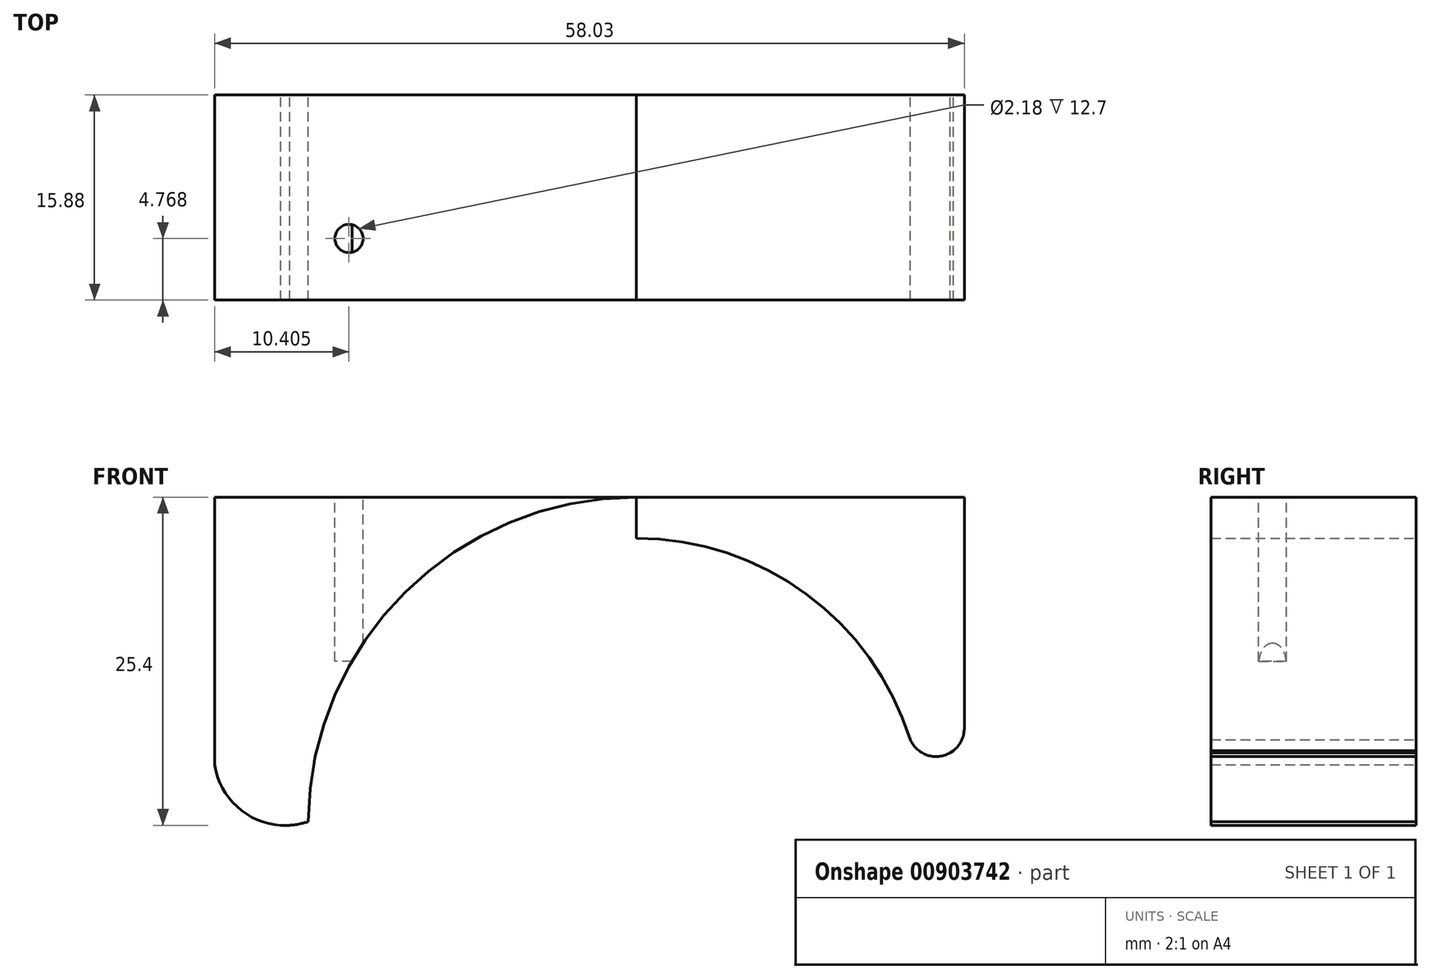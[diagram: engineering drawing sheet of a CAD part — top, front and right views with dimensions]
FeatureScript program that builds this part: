
annotation { "Feature Type Name" : "Feature", "Feature Type Description" : "" }
export const myFeature = defineFeature(function(context is Context, id is Id, definition is map)
    precondition{}
    {
        {
            var Q0;
            Q0=qCreatedBy(makeId("Front.planeOp"),FACE);
            var sketch = newSketch(context, id + "F0", { "sketchPlane" : qUnion([Q0])});
            skCircle(sketch, "E0", {"center": v(0, 0) * mm, "radius": 22.23 * mm});
            skCircle(sketch, "E1", {"center": v(0, 0) * mm, "radius": 25.4 * mm});
            skLineSegment(sketch, "E2.bottom", {"start": v(-25.4, 0) * mm, "end": v(0, 0) * mm});
            skLineSegment(sketch, "E2.top", {"start": v(-25.4, 25.4) * mm, "end": v(0, 25.4) * mm});
            skLineSegment(sketch, "E2.right", {"start": v(0, 0) * mm, "end": v(0, 25.4) * mm});
            skLineSegment(sketch, "E3.bottom", {"start": v(25.4, 0) * mm, "end": v(0, 0) * mm});
            skLineSegment(sketch, "E3.top", {"start": v(25.4, 25.4) * mm, "end": v(0, 25.4) * mm});
            skLineSegment(sketch, "E3.left", {"start": v(25.4, 0) * mm, "end": v(25.4, 25.4) * mm});
            skLineSegment(sketch, "E4", {"start": v(-25.4, 0) * mm, "end": v(-32.63, 0) * mm});
            skLineSegment(sketch, "E5", {"start": v(-32.63, 0) * mm, "end": v(-32.63, 25.4) * mm});
            skLineSegment(sketch, "E6", {"start": v(-32.63, 25.4) * mm, "end": v(-25.4, 25.4) * mm});
            skCircle(sketch, "E7", {"center": v(-27.16, 5.52) * mm, "radius": 5.53 * mm});
            skPoint(sketch, "E7.first.point", {"position": v(-32.63, 4.68) * mm});
            skPoint(sketch, "E7.second.point", {"position": v(-27.5, 0) * mm});
            skPoint(sketch, "E7.third.point", {"position": v(-21.88, 3.87) * mm});
            skLineSegment(sketch, "E8", {"start": v(21.87, 3.98) * mm, "end": v(25.4, 6.34) * mm});
            skCircle(sketch, "E9", {"center": v(23.22, 7.5) * mm, "radius": 2.18 * mm});
            skPoint(sketch, "E9.first.point", {"position": v(25.4, 7.5) * mm});
            skPoint(sketch, "E9.second.point", {"position": v(24.3, 5.6) * mm});
            skPoint(sketch, "E9.third.point", {"position": v(21.08, 7.03) * mm});
            skSolve(sketch);
        }
        {
            var Q0;
            {var subQ0=sQuery(id+"F0.wireOp",EDGE,"E7");var subQ6=sQuery(id+"F0.wireOp",EDGE,"E1");var subQ9=makeQuery(id+"F0.imprint","INTERSECT",VERTEX,{"disambiguationData":[OD(0.0)],"derivedFrom":[subQ6,subQ0]});Q0=makeQuery(id+"F0.imprint","IMPRINT",FACE,{"disambiguationData":[TD([[makeQuery(id+"F0.imprint","IMPRINT",EDGE,{"disambiguationData":[TD([[subQ9,-1.0]])],"derivedFrom":subQ6}),-1.0]])]});}
            var Q1;
            {var subQ0=sQuery(id+"F0.wireOp",EDGE,"E7");var subQ1=makeQuery(id+"F0.imprint","IMPRINT",VERTEX,{"derivedFrom":subQ0});Q1=makeQuery(id+"F0.imprint","IMPRINT",FACE,{"disambiguationData":[TD([[makeQuery(id+"F0.imprint","IMPRINT",EDGE,{"disambiguationData":[TD([[subQ1,1.0]])],"derivedFrom":subQ0}),1.0]])]});}
            var Q2;
            {var subQ5=sQuery(id+"F0.wireOp",EDGE,"E7");var subQ6=makeQuery(id+"F0.imprint","IMPRINT",VERTEX,{"derivedFrom":subQ5});Q2=makeQuery(id+"F0.imprint","IMPRINT",FACE,{"disambiguationData":[TD([[makeQuery(id+"F0.imprint","IMPRINT",EDGE,{"disambiguationData":[TD([[subQ6,1.0]])],"derivedFrom":subQ5}),-1.0]])]});}
            var Q3;
            {var subQ0=sQuery(id+"F0.wireOp",EDGE,"E9");var subQ1=sQuery(id+"F0.wireOp",EDGE,"E0");var subQ2=makeQuery(id+"F0.imprint","INTERSECT",VERTEX,{"disambiguationData":[OD(1.0)],"derivedFrom":[subQ1,subQ0]});Q3=makeQuery(id+"F0.imprint","IMPRINT",FACE,{"disambiguationData":[TD([[makeQuery(id+"F0.imprint","IMPRINT",EDGE,{"disambiguationData":[TD([[subQ2,-1.0]])],"derivedFrom":subQ1}),-1.0]])]});}
            var Q4;
            {var subQ0=sQuery(id+"F0.wireOp",EDGE,"E9");var subQ7=sQuery(id+"F0.wireOp",EDGE,"E0");var subQ8=makeQuery(id+"F0.imprint","INTERSECT",VERTEX,{"disambiguationData":[OD(0.0)],"derivedFrom":[subQ7,subQ0]});Q4=makeQuery(id+"F0.imprint","IMPRINT",FACE,{"disambiguationData":[TD([[makeQuery(id+"F0.imprint","IMPRINT",EDGE,{"disambiguationData":[TD([[subQ8,-1.0]])],"derivedFrom":subQ7}),-1.0]])]});}
            var Q5;
            {var subQ0=sQuery(id+"F0.wireOp",EDGE,"E9");var subQ1=sQuery(id+"F0.wireOp",EDGE,"E1");var subQ2=makeQuery(id+"F0.imprint","INTERSECT",VERTEX,{"disambiguationData":[OD(0.0)],"derivedFrom":[subQ1,subQ0]});Q5=makeQuery(id+"F0.imprint","IMPRINT",FACE,{"disambiguationData":[TD([[makeQuery(id+"F0.imprint","IMPRINT",EDGE,{"disambiguationData":[TD([[subQ2,-1.0]])],"derivedFrom":subQ1}),-1.0]])]});}
            var Q6;
            {var subQ0=sQuery(id+"F0.wireOp",EDGE,"E3.top");Q6=makeQuery(id+"F0.imprint","IMPRINT",FACE,{"disambiguationData":[TD([[makeQuery(id+"F0.imprint","IMPRINT",EDGE,{"derivedFrom":subQ0}),1.0]])]});}
            var Q7;
            {var subQ4=sQuery(id+"F0.wireOp",EDGE,"E2.top");Q7=makeQuery(id+"F0.imprint","IMPRINT",FACE,{"disambiguationData":[TD([[makeQuery(id+"F0.imprint","IMPRINT",EDGE,{"derivedFrom":subQ4}),-1.0]])]});}
            extrude(context, id + "F1", {"entities" : qUnion([Q0, Q1, Q2, Q3, Q4, Q5, Q6, Q7]), "depth" : 15.88 * mm, "offsetDistance" : 25.4 * mm});
        }
        {
            var Q0;
            Q0=makeQuery(id+"F1.opExtrude","SWEPT_FACE",FACE,{"disambiguationData":[OSD([sQuery(id+"F0.wireOp",EDGE,"E2.top"),sQuery(id+"F0.wireOp",EDGE,"E3.top"),sQuery(id+"F0.wireOp",EDGE,"E6")])]});
            var sketch = newSketch(context, id + "F2", { "sketchPlane" : qUnion([Q0])});
            skCircle(sketch, "E10", {"center": v(-22.23, -11.11) * mm, "radius": 1.1 * mm});
            skLineSegment(sketch, "E11.0", {"start": v(25.4, -15.88) * mm, "end": v(-32.63, -15.88) * mm, "construction": true});
            skPoint(sketch, "E12.0", {"position": v(0, 0) * mm});
            skSolve(sketch);
        }
        {
            var Q0;
            Q0=makeQuery(id+"F2.imprint","IMPRINT",FACE,{"disambiguationData":[TD([[makeQuery(id+"F2.imprint","IMPRINT",EDGE,{"derivedFrom":sQuery(id+"F2.wireOp",EDGE,"E10")}),1.0]])]});
            extrude(context, id + "F3", {"entities" : qUnion([Q0]), "operationType" : NewBodyOperationType.REMOVE, "oppositeDirection" : true, "depth" : 12.7 * mm, "offsetDistance" : 25.4 * mm});
        }
    });
